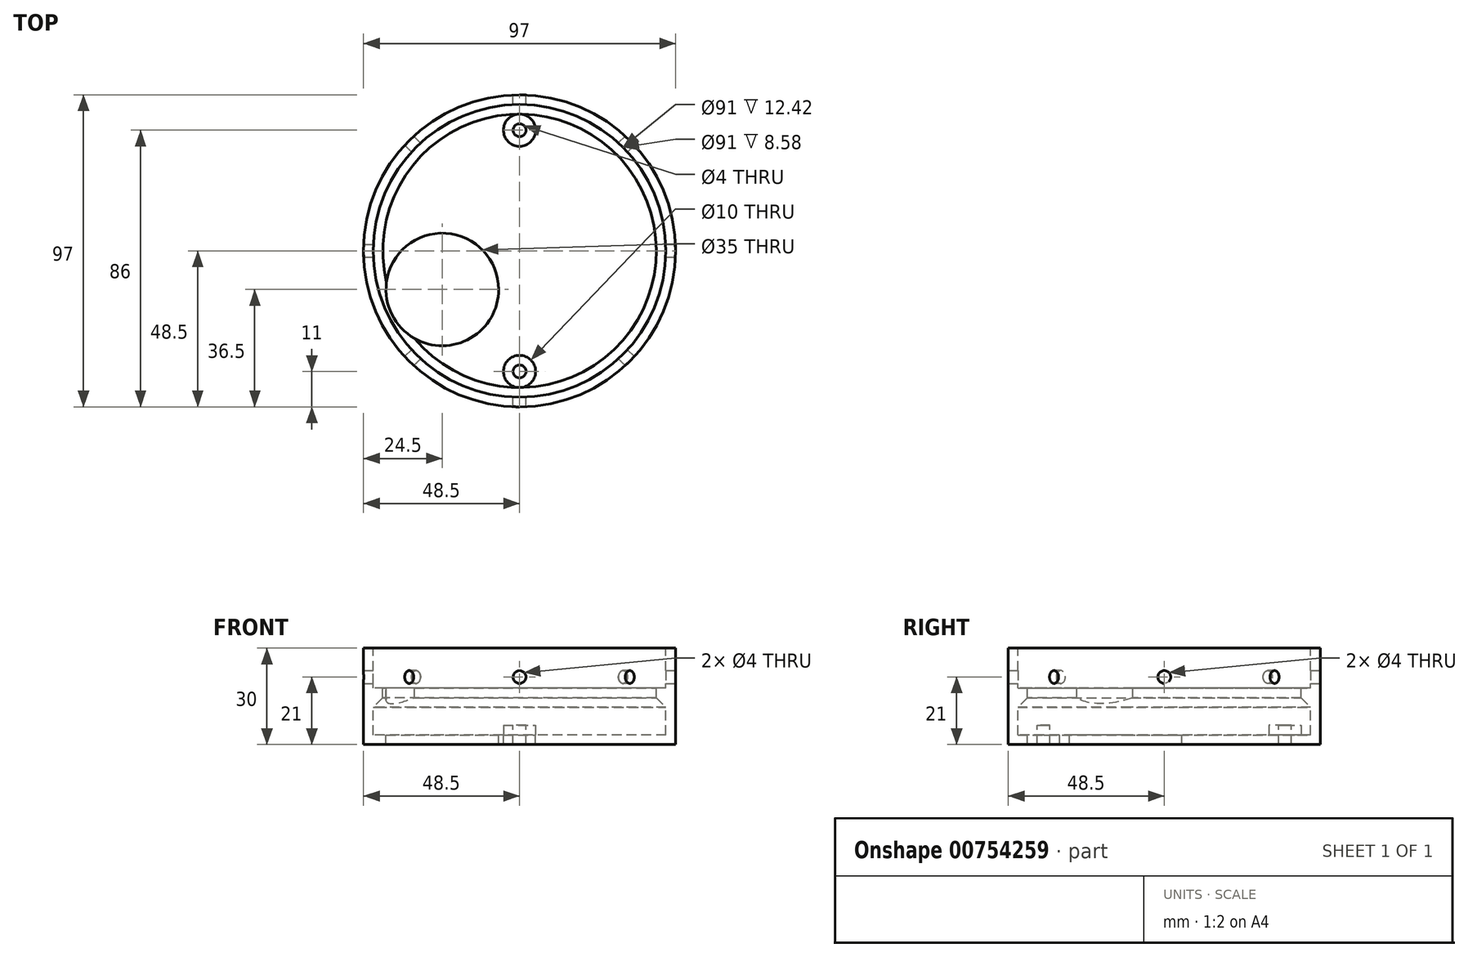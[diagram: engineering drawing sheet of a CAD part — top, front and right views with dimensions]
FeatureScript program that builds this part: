
annotation { "Feature Type Name" : "Feature", "Feature Type Description" : "" }
export const myFeature = defineFeature(function(context is Context, id is Id, definition is map)
    precondition{}
    {
        {
            var Q0;
            Q0=qCreatedBy(makeId("Front.planeOp"),FACE);
            var sketch = newSketch(context, id + "F0", { "sketchPlane" : qUnion([Q0])});
            skLineSegment(sketch, "E0", {"start": v(0, 0) * mm, "end": v(-48.5, 0) * mm});
            skLineSegment(sketch, "E1", {"start": v(-48.5, 0) * mm, "end": v(-48.5, 30) * mm});
            skLineSegment(sketch, "E2", {"start": v(-48.5, 30) * mm, "end": v(-45.5, 30) * mm});
            skLineSegment(sketch, "E3", {"start": v(-45.5, 30) * mm, "end": v(-45.5, 3) * mm});
            skLineSegment(sketch, "E4", {"start": v(-45.5, 3) * mm, "end": v(0, 3) * mm});
            skLineSegment(sketch, "E5", {"start": v(0, 3) * mm, "end": v(0, 0) * mm});
            skLineSegment(sketch, "E6", {"start": v(0, 0) * mm, "end": v(0, 34.93) * mm, "construction": true});
            skLineSegment(sketch, "E7", {"start": v(-45.5, 17.58) * mm, "end": v(-42.5, 17.58) * mm});
            skLineSegment(sketch, "E8", {"start": v(-42.5, 17.58) * mm, "end": v(-42.5, 14.58) * mm});
            skLineSegment(sketch, "E9", {"start": v(-42.5, 14.58) * mm, "end": v(-45.5, 11.58) * mm});
            skPoint(sketch, "E10", {"position": v(-45.5, 16.5) * mm});
            skSolve(sketch);
        }
        {
            var Q0;
            Q0=makeQuery(id+"F0.imprint","IMPRINT",FACE,{"disambiguationData":[TD([[makeQuery(id+"F0.imprint","IMPRINT",EDGE,{"derivedFrom":sQuery(id+"F0.wireOp",EDGE,"E0")}),-1.0]])]});
            var Q1;
            {var subQ0=sQuery(id+"F0.wireOp",EDGE,"E7");Q1=makeQuery(id+"F0.imprint","IMPRINT",FACE,{"disambiguationData":[TD([[makeQuery(id+"F0.imprint","IMPRINT",EDGE,{"derivedFrom":subQ0}),-1.0]])]});}
            var Q2;
            Q2=sQuery(id+"F0.wireOp",EDGE,"E5");
            revolve(context, id + "F1", {"surfaceOperationType" : NewSurfaceOperationType.NEW, "entities" : qUnion([Q0, Q1]), "axis" : qUnion([Q2]), "revolveType" : RevolveType.FULL});
        }
        {
            var Q0;
            Q0=qCreatedBy(makeId("Front.planeOp"),FACE);
            var sketch = newSketch(context, id + "F2", { "sketchPlane" : qUnion([Q0])});
            skCircle(sketch, "E11", {"center": v(0, 21) * mm, "radius": 2 * mm});
            skSolve(sketch);
        }
        {
            var Q0;
            Q0=makeQuery(id+"F2.imprint","IMPRINT",FACE,{"disambiguationData":[TD([[makeQuery(id+"F2.imprint","IMPRINT",EDGE,{"derivedFrom":sQuery(id+"F2.wireOp",EDGE,"E11")}),1.0]])]});
            extrude(context, id + "F3", {"entities" : qUnion([Q0]), "operationType" : NewBodyOperationType.REMOVE, "endBound" : BoundingType.SYMMETRIC, "depth" : 155.6 * mm, "offsetDistance" : 25 * mm});
        }
        {
            var Q0;
            Q0=qCreatedBy(makeId("Top.planeOp"),FACE);
            var sketch = newSketch(context, id + "F4", { "sketchPlane" : qUnion([Q0])});
            skCircle(sketch, "E12", {"center": v(0, -37.5) * mm, "radius": 5 * mm});
            skCircle(sketch, "E13.MirrorC", {"center": v(0, 37.5) * mm, "radius": 5 * mm});
            skSolve(sketch);
        }
        {
            var Q0;
            Q0 = qSketchRegion(id + "F4", true);
            extrude(context, id + "F5", {"entities" : qUnion([Q0]), "operationType" : NewBodyOperationType.ADD, "depth" : 6 * mm, "offsetDistance" : 25 * mm});
        }
        {
            var Q0;
            Q0=makeQuery(id+"F1.opRevolve","SWEPT_FACE",FACE,{"disambiguationData":[OSD([sQuery(id+"F0.wireOp",EDGE,"E4")])]});
            var sketch = newSketch(context, id + "F6", { "sketchPlane" : qUnion([Q0])});
            skCircle(sketch, "E14", {"center": v(0, 37.5) * mm, "radius": 2 * mm});
            skLineSegment(sketch, "E15", {"start": v(0, 0) * mm, "end": v(-20, 0) * mm, "construction": true});
            skCircle(sketch, "E16.MirrorC", {"center": v(0, -37.5) * mm, "radius": 2 * mm});
            skSolve(sketch);
        }
        {
            var Q0;
            Q0=makeQuery(id+"F6.imprint","IMPRINT",FACE,{"disambiguationData":[TD([[makeQuery(id+"F6.imprint","IMPRINT",EDGE,{"derivedFrom":sQuery(id+"F6.wireOp",EDGE,"E14")}),1.0]])]});
            extrude(context, id + "F7", {"entities" : qUnion([Q0]), "operationType" : NewBodyOperationType.REMOVE, "endBound" : BoundingType.SYMMETRIC, "oppositeDirection" : true, "depth" : 25 * mm, "offsetDistance" : 25 * mm});
        }
        {
            var Q0;
            Q0=makeQuery(id+"F6.imprint","IMPRINT",FACE,{"disambiguationData":[TD([[makeQuery(id+"F6.imprint","IMPRINT",EDGE,{"derivedFrom":sQuery(id+"F6.wireOp",EDGE,"E16.MirrorC")}),-1.0]])]});
            extrude(context, id + "F8", {"entities" : qUnion([Q0]), "operationType" : NewBodyOperationType.REMOVE, "endBound" : BoundingType.SYMMETRIC, "oppositeDirection" : true, "depth" : 25 * mm, "offsetDistance" : 25 * mm});
        }
        {
            var Q0;
            Q0=qCreatedBy(makeId("Right.planeOp"),FACE);
            var sketch = newSketch(context, id + "F9", { "sketchPlane" : qUnion([Q0])});
            skCircle(sketch, "E17", {"center": v(0, 21) * mm, "radius": 2 * mm});
            skSolve(sketch);
        }
        {
            var Q0;
            Q0=makeQuery(id+"F9.imprint","IMPRINT",FACE,{"disambiguationData":[TD([[makeQuery(id+"F9.imprint","IMPRINT",EDGE,{"derivedFrom":sQuery(id+"F9.wireOp",EDGE,"E17")}),1.0]])]});
            extrude(context, id + "F10", {"entities" : qUnion([Q0]), "operationType" : NewBodyOperationType.REMOVE, "endBound" : BoundingType.SYMMETRIC, "oppositeDirection" : true, "depth" : 100 * mm, "offsetDistance" : 25 * mm});
        }
        {
            var Q0;
            {var subQ0=sQuery(id+"F0.wireOp",EDGE,"E4");Q0=makeQuery(id+"F6.imprint","IMPRINT",FACE,{"disambiguationData":[TD([[makeQuery(id+"F6.imprint","IMPRINT",EDGE,{"derivedFrom":makeQuery(id+"F1.opRevolve","SWEPT_EDGE",EDGE,{"disambiguationData":[OSD([sQuery(id+"F0.wireOp",EDGE,"E3"),subQ0])]})}),1.0]])]});}
            var sketch = newSketch(context, id + "F11", { "sketchPlane" : qUnion([Q0])});
            skCircle(sketch, "E18", {"center": v(-24, -12) * mm, "radius": 17.5 * mm});
            skLineSegment(sketch, "E19", {"start": v(0, 0) * mm, "end": v(0, -30) * mm, "construction": true});
            skSolve(sketch);
        }
        {
            var Q0;
            Q0 = qSketchRegion(id + "F11", true);
            extrude(context, id + "F12", {"entities" : qUnion([Q0]), "operationType" : NewBodyOperationType.REMOVE, "endBound" : BoundingType.SYMMETRIC, "oppositeDirection" : true, "depth" : 50 * mm, "offsetDistance" : 25 * mm});
        }
        {
            var Q0;
            Q0=qCreatedBy(makeId("Right.planeOp"),FACE);
            var Q1;
            Q1=sQuery(id+"F0.wireOp",EDGE,"E6");
            cPlane(context, id + "F13", {"entities" : qUnion([Q0, Q1]), "cplaneType" : CPlaneType.LINE_ANGLE, "offset" : 25 * mm, "angle" : 45 * degree, "width" : 150 * mm, "height" : 150 * mm});
        }
        {
            var Q0;
            Q0=qCreatedBy(id+"F13.planeOp",FACE);
            var sketch = newSketch(context, id + "F14", { "sketchPlane" : qUnion([Q0])});
            skCircle(sketch, "E20", {"center": v(0, 21) * mm, "radius": 2 * mm});
            skSolve(sketch);
        }
        {
            var Q0;
            Q0 = qSketchRegion(id + "F14", true);
            extrude(context, id + "F15", {"entities" : qUnion([Q0]), "operationType" : NewBodyOperationType.REMOVE, "endBound" : BoundingType.SYMMETRIC, "oppositeDirection" : true, "depth" : 100 * mm, "offsetDistance" : 25 * mm});
        }
        {
            var Q0;
            Q0=qCreatedBy(id+"F13.planeOp",FACE);
            var Q1;
            Q1=sQuery(id+"F0.wireOp",EDGE,"E6");
            cPlane(context, id + "F16", {"entities" : qUnion([Q0, Q1]), "cplaneType" : CPlaneType.LINE_ANGLE, "offset" : 25 * mm, "angle" : 90 * degree, "width" : 150 * mm, "height" : 150 * mm});
        }
        {
            var Q0;
            Q0=qCreatedBy(id+"F16.planeOp",FACE);
            var sketch = newSketch(context, id + "F17", { "sketchPlane" : qUnion([Q0])});
            skCircle(sketch, "E21", {"center": v(0, 21) * mm, "radius": 2 * mm});
            skSolve(sketch);
        }
        {
            var Q0;
            Q0 = qSketchRegion(id + "F17", true);
            extrude(context, id + "F18", {"entities" : qUnion([Q0]), "operationType" : NewBodyOperationType.REMOVE, "endBound" : BoundingType.SYMMETRIC, "oppositeDirection" : true, "depth" : 100 * mm, "offsetDistance" : 25 * mm});
        }
    });
